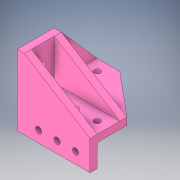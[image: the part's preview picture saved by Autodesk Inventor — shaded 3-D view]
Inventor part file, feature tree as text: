
AUTODESK INVENTOR PART (.ipt)
format: ipt  version: 2019 (Build 230136000, 136)  size: 212,480 bytes
history: native  units: in
note: dims shown in document units (in); Inventor stores cm internally (conversion verified against a paired STEP export)
features: extrude x8, sketch x8, projected_geometry x2, plane x1
ambient origin geometry x8: Origin, YZ Plane, XZ Plane, XY Plane, X Axis, Y Axis, Z Axis, Center Point
bodies: Solid1 (feature_tree)
feature tree (19):
  extrude  "Extrusion1"  Depth=0.7874in
  extrude  "Extrusion2"  Depth=0.25in
  extrude  "Extrusion3"  Depth=2.4528in TaperAngle=0.0deg
  plane  "Work Plane1"
  extrude  "Extrusion4"  Depth=0.7874in
  extrude  "Extrusion5"  Depth=2.4528in TaperAngle=0.0deg
  extrude  "Extrusion7"  Depth=0.3937in
  extrude  "Extrusion8"  Depth=0.3937in
  extrude  "Extrusion9"  [1 undecoded]
  sketch  "Sketch1"  dims[d0=1.5in d1=0.7874in]
  sketch  "Sketch2"  dims[d2=0.7874in d3=0.25in]
  sketch  "Sketch3"  dims[d4=0.25in d5=2.4528in d6=0.0in]
  sketch  "Sketch4"  dims[d7=0.7874in d8=0.2165in]
  projected_geometry  "Projected Loop1"
  sketch  "Sketch5"  dims[d10=1.1811in d12=0.6437in d13=0.3937in d15=1.0in d17=2.4528in d18=0.0in]
  sketch  "Sketch7"  dims[d19=0.3937in d20=0.2165in]
  sketch  "Sketch8"  dims[d21=0.5in d22=1.1811in d24=0.6437in d25=0.3937in d27=1.0in]
  projected_geometry  "Projected Loop2"
  sketch  "Sketch9"  dims[d29=2.4528in d30=0.0in d31=-0.7874in d32=0.7874in d33=1.1811in d35=0.75in d36=0.3937in d38=1.0in d40=0.2165in d41=1.1811in d43=0.75in d44=0.3937in d46=1.0in d48=0.25in d49=0.0in d50=0.25in d51=0.25in d52=0.25in d53=0.0in d59=0.25in d60=0.0in d61=0.25in d62=0.0in d63=0.9827in d64=0.2165in d65=0.25in d66=0.0in d67=0.0in d68=0.5in d69=0.0in]
note: 1 required parameter value undecoded (feature->parameter linkage not recoverable at this tier; creation-order binding heuristic only, values carry confidence <= 0.55)
